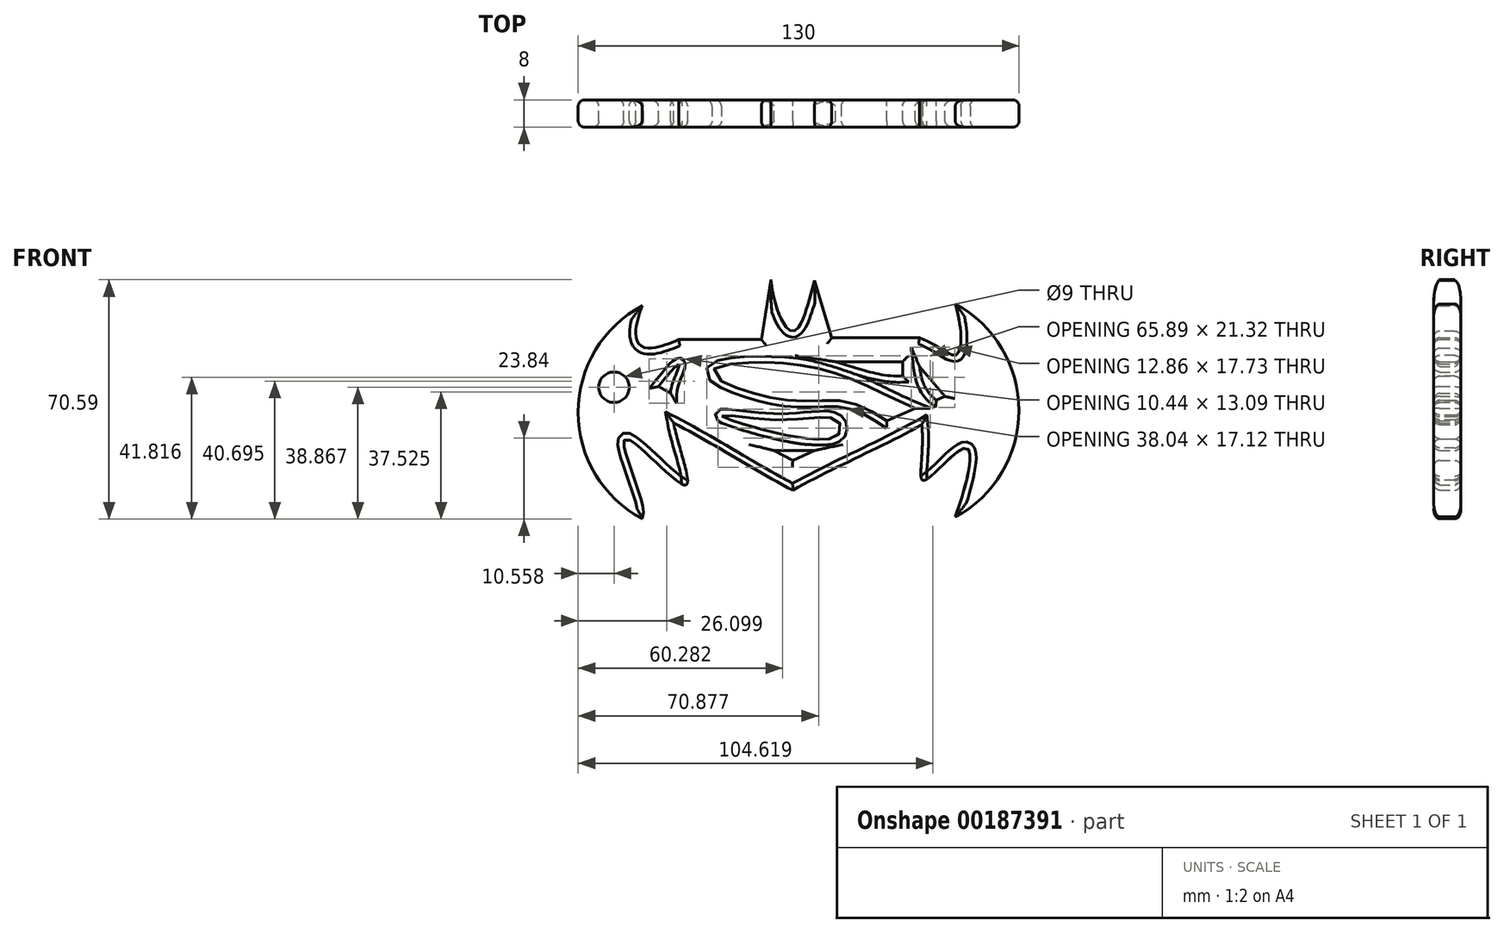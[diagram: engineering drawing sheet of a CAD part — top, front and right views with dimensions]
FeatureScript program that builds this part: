
annotation { "Feature Type Name" : "Feature", "Feature Type Description" : "" }
export const myFeature = defineFeature(function(context is Context, id is Id, definition is map)
    precondition{}
    {
        {
            var Q0;
            Q0=qCreatedBy(makeId("Front.planeOp"),FACE);
            var sketch = newSketch(context, id + "F0", { "sketchPlane" : qUnion([Q0])});
            skLineSegment(sketch, "E0", {"start": v(-12.91, 41.7) * mm, "end": v(-15.72, 24) * mm});
            skLineSegment(sketch, "E1", {"start": v(0, 41.41) * mm, "end": v(5.05, 24.57) * mm});
            skFitSpline(sketch, "E2", {"points": [v(-12.91, 41.7) * mm, v(-6.46, 26.53) * mm, v(0, 41.41) * mm], "startDerivative": vector(5.25, -48.76) * mm, "endDerivative": vector(12.88, 47.63) * mm});
            skLineSegment(sketch, "E3", {"start": v(-15.72, 24) * mm, "end": v(-40.11, 24) * mm});
            skLineSegment(sketch, "E4", {"start": v(5.05, 24.57) * mm, "end": v(30.98, 24.57) * mm});
            skFitSpline(sketch, "E5", {"points": [v(-40.11, 24) * mm, v(-51.3, 22.22) * mm, v(-50.91, 33.97) * mm], "startDerivative": vector(-39.59, -16.97) * mm, "endDerivative": vector(15.78, 44.08) * mm});
            skFitSpline(sketch, "E6", {"points": [v(30.98, 24.57) * mm, v(41.82, 19.47) * mm, v(41.48, 34.5) * mm], "startDerivative": vector(43.18, -18.5) * mm, "endDerivative": vector(-13.44, 48.11) * mm});
            skFitSpline(sketch, "E7", {"points": [v(41.48, -28.3) * mm, v(44.06, -8) * mm, v(32.34, -17.5) * mm, v(31.6, -1.1) * mm], "startDerivative": vector(35.63, 101) * mm, "endDerivative": vector(-8, 85.3) * mm});
            skFitSpline(sketch, "E8", {"points": [v(-50.91, -28.83) * mm, v(-50.91, -24.08) * mm, v(-55.7, -5.25) * mm, v(-38.31, -18.9) * mm, v(-41.58, -0.55) * mm], "startDerivative": vector(6.87, 19.6) * mm, "endDerivative": vector(-14.48, 80.7) * mm});
            skFitSpline(sketch, "E9", {"points": [v(-41.58, -0.55) * mm, v(-6.46, -20.38) * mm], "startDerivative": vector(37.07, -19.28) * mm, "endDerivative": vector(37.07, -19.28) * mm});
            skFitSpline(sketch, "E10", {"points": [v(31.6, -1.1) * mm, v(-6.46, -20.38) * mm], "startDerivative": vector(-37.45, -20.69) * mm, "endDerivative": vector(-37.45, -20.69) * mm});
            skLineSegment(sketch, "E11", {"start": v(-6.46, -15.44) * mm, "end": v(41.82, 6.41) * mm});
            skLineSegment(sketch, "E12", {"start": v(41.82, 6.41) * mm, "end": v(30.98, 21.66) * mm});
            skLineSegment(sketch, "E13", {"start": v(30.98, 21.66) * mm, "end": v(-40.11, 21.2) * mm});
            skLineSegment(sketch, "E14", {"start": v(-40.11, 21.2) * mm, "end": v(-51.3, 8.73) * mm});
            skLineSegment(sketch, "E15", {"start": v(-51.3, 8.73) * mm, "end": v(-6.46, -15.44) * mm});
            skArc(sketch, "E16", {"start": v(-50.91, 33.97) * mm, "mid": v(-69.72, 2.57) * mm, "end": v(-50.91, -28.83) * mm});
            skArc(sketch, "E17", {"start": v(41.48, -28.3) * mm, "mid": v(60.28, 3.1) * mm, "end": v(41.48, 34.5) * mm});
            skLineSegment(sketch, "E18", {"start": v(-6.46, -11.62) * mm, "end": v(0, -8.7) * mm});
            skLineSegment(sketch, "E19", {"start": v(0, -8.7) * mm, "end": v(-12.03, -8.7) * mm});
            skLineSegment(sketch, "E20", {"start": v(-12.03, -8.7) * mm, "end": v(-6.46, -11.62) * mm});
            skFitSpline(sketch, "E21", {"points": [v(-27.4, 1.5) * mm, v(-10.6, 0.35) * mm, v(6.93, 0) * mm, v(5.75, -4.85) * mm, v(-27.4, 1.5) * mm]});
            skLineSegment(sketch, "E22", {"start": v(-46.08, 10.16) * mm, "end": v(-42.51, 8.24) * mm});
            skLineSegment(sketch, "E23", {"start": v(35.92, 6.14) * mm, "end": v(38.41, 7.27) * mm});
            skLineSegment(sketch, "E24", {"start": v(38.41, 7.27) * mm, "end": v(30.96, 16.07) * mm});
            skFitSpline(sketch, "E25", {"points": [v(30.96, 16.07) * mm, v(35.92, 6.14) * mm], "startDerivative": vector(1.42, -12.05) * mm, "endDerivative": vector(10.63, -8.5) * mm});
            skLineSegment(sketch, "E26", {"start": v(25.93, 17.49) * mm, "end": v(25.96, 13.23) * mm});
            skLineSegment(sketch, "E27", {"start": v(25.96, 13.23) * mm, "end": v(25.93, 17.49) * mm});
            skLineSegment(sketch, "E28", {"start": v(6.14, 17.49) * mm, "end": v(25.93, 17.49) * mm});
            skFitSpline(sketch, "E29", {"points": [v(6.14, 17.49) * mm, v(25.96, 13.23) * mm], "startDerivative": vector(18.43, -5.67) * mm, "endDerivative": vector(19.75, 0.7) * mm});
            skLineSegment(sketch, "E30", {"start": v(21.34, 0) * mm, "end": v(29.64, 3.76) * mm});
            skFitSpline(sketch, "E31", {"points": [v(29.64, 3.76) * mm, v(-2.9, 16.3) * mm, v(-30.27, 14.52) * mm, v(-9.16, 6.26) * mm, v(8.78, 5.78) * mm, v(16.3, 3.13) * mm, v(21.34, 0) * mm], "startDerivative": vector(-155.46, 66.73) * mm, "endDerivative": vector(157.37, -97.92) * mm});
            skFitSpline(sketch, "E32", {"points": [v(-46.08, 10.16) * mm, v(-39.94, 16.69) * mm, v(-42.51, 8.24) * mm], "startDerivative": vector(16.59, 20.52) * mm, "endDerivative": vector(-0.25, -15.84) * mm});
            skCircle(sketch, "E33", {"center": v(-59.16, 9.97) * mm, "radius": 4.5 * mm});
            skSolve(sketch);
        }
        {
            var Q0;
            Q0=makeQuery(id+"F0.imprint","IMPRINT",FACE,{"disambiguationData":[TD([[makeQuery(id+"F0.imprint","IMPRINT",EDGE,{"derivedFrom":sQuery(id+"F0.wireOp",EDGE,"E11")}),1.0]])]});
            var Q1;
            Q1=makeQuery(id+"F0.imprint","IMPRINT",FACE,{"disambiguationData":[TD([[makeQuery(id+"F0.imprint","IMPRINT",EDGE,{"derivedFrom":sQuery(id+"F0.wireOp",EDGE,"E0")}),1.0]])]});
            extrude(context, id + "F1", {"entities" : qUnion([Q0, Q1]), "depth" : 8 * mm});
        }
        {
            var Q0;
            Q0=makeQuery(id+"F1.opExtrude","CAP_FACE",FACE,{"disambiguationData":[OSD([sQuery(id+"F0.wireOp",EDGE,"E0"),sQuery(id+"F0.wireOp",EDGE,"E1"),sQuery(id+"F0.wireOp",EDGE,"E2"),sQuery(id+"F0.wireOp",EDGE,"E3"),sQuery(id+"F0.wireOp",EDGE,"E4"),sQuery(id+"F0.wireOp",EDGE,"E5"),sQuery(id+"F0.wireOp",EDGE,"E6"),sQuery(id+"F0.wireOp",EDGE,"E7"),sQuery(id+"F0.wireOp",EDGE,"E8"),sQuery(id+"F0.wireOp",EDGE,"E9"),sQuery(id+"F0.wireOp",EDGE,"E10"),sQuery(id+"F0.wireOp",EDGE,"E16"),sQuery(id+"F0.wireOp",EDGE,"E17"),sQuery(id+"F0.wireOp",EDGE,"E18"),sQuery(id+"F0.wireOp",EDGE,"E19"),sQuery(id+"F0.wireOp",EDGE,"E20"),sQuery(id+"F0.wireOp",EDGE,"E21"),sQuery(id+"F0.wireOp",EDGE,"E22"),sQuery(id+"F0.wireOp",EDGE,"E23"),sQuery(id+"F0.wireOp",EDGE,"E24"),sQuery(id+"F0.wireOp",EDGE,"E25"),sQuery(id+"F0.wireOp",EDGE,"E27"),sQuery(id+"F0.wireOp",EDGE,"E28"),sQuery(id+"F0.wireOp",EDGE,"E29"),sQuery(id+"F0.wireOp",EDGE,"E30"),sQuery(id+"F0.wireOp",EDGE,"E31"),sQuery(id+"F0.wireOp",EDGE,"E32")])],"isStart":false});
            var Q1;
            Q1=makeQuery(id+"F1.opExtrude","CAP_FACE",FACE,{"disambiguationData":[OSD([sQuery(id+"F0.wireOp",EDGE,"E0"),sQuery(id+"F0.wireOp",EDGE,"E1"),sQuery(id+"F0.wireOp",EDGE,"E2"),sQuery(id+"F0.wireOp",EDGE,"E3"),sQuery(id+"F0.wireOp",EDGE,"E4"),sQuery(id+"F0.wireOp",EDGE,"E5"),sQuery(id+"F0.wireOp",EDGE,"E6"),sQuery(id+"F0.wireOp",EDGE,"E7"),sQuery(id+"F0.wireOp",EDGE,"E8"),sQuery(id+"F0.wireOp",EDGE,"E9"),sQuery(id+"F0.wireOp",EDGE,"E10"),sQuery(id+"F0.wireOp",EDGE,"E16"),sQuery(id+"F0.wireOp",EDGE,"E17"),sQuery(id+"F0.wireOp",EDGE,"E18"),sQuery(id+"F0.wireOp",EDGE,"E19"),sQuery(id+"F0.wireOp",EDGE,"E20"),sQuery(id+"F0.wireOp",EDGE,"E21"),sQuery(id+"F0.wireOp",EDGE,"E22"),sQuery(id+"F0.wireOp",EDGE,"E23"),sQuery(id+"F0.wireOp",EDGE,"E24"),sQuery(id+"F0.wireOp",EDGE,"E25"),sQuery(id+"F0.wireOp",EDGE,"E27"),sQuery(id+"F0.wireOp",EDGE,"E28"),sQuery(id+"F0.wireOp",EDGE,"E29"),sQuery(id+"F0.wireOp",EDGE,"E30"),sQuery(id+"F0.wireOp",EDGE,"E31"),sQuery(id+"F0.wireOp",EDGE,"E32")])],"isStart":true});
            fillet(context, id + "F2", {"entities" : qUnion([Q0, Q1]), "radius" : 1.8 * mm, "tangentPropagation" : true, "allowEdgeOverflow" : false});
        }
    });
